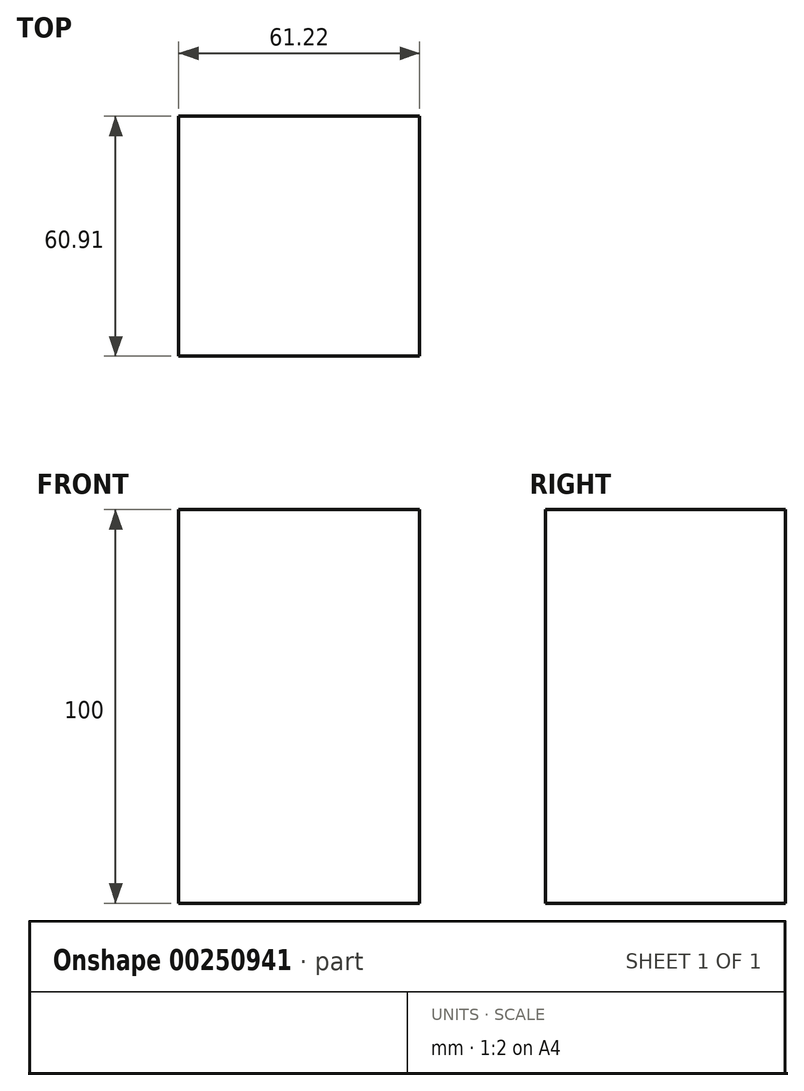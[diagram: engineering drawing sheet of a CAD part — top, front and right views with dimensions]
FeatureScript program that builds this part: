
annotation { "Feature Type Name" : "Feature", "Feature Type Description" : "" }
export const myFeature = defineFeature(function(context is Context, id is Id, definition is map)
    precondition{}
    {
        {
            var Q0;
            Q0=qCreatedBy(makeId("Top.planeOp"),FACE);
            var sketch = newSketch(context, id + "F0", { "sketchPlane" : qUnion([Q0])});
            skLineSegment(sketch, "E0", {"start": v(-51.76, 45.35) * mm, "end": v(-51.76, -16.49) * mm});
            skLineSegment(sketch, "E1", {"start": v(-51.76, -16.49) * mm, "end": v(9.46, -16.49) * mm});
            skLineSegment(sketch, "E2", {"start": v(9.46, -16.49) * mm, "end": v(9.46, 44.42) * mm});
            skLineSegment(sketch, "E3", {"start": v(9.46, 44.42) * mm, "end": v(-55.49, 44.42) * mm});
            skSolve(sketch);
        }
        {
            var Q0;
            {var subQ0=sQuery(id+"F0.wireOp",EDGE,"E1");Q0=makeQuery(id+"F0.imprint","IMPRINT",FACE,{"disambiguationData":[TD([[makeQuery(id+"F0.imprint","IMPRINT",EDGE,{"derivedFrom":subQ0}),1.0]])]});}
            extrude(context, id + "F1", {"entities" : qUnion([Q0]), "endBound" : BoundingType.SYMMETRIC, "depth" : 100 * mm});
        }
    });
